# Revit family: Curved Walls U-Profile
name_source: partatom
category: Generic Models
revit_build: Autodesk Revit 2016 (Build: 20160217_1800(x64)
units: mm (PartAtom-declared; Revit-internal decimal feet)

## family parameters
Always vertical = No
Can host rebar = No
Cut with Voids When Loaded = No
Part Type = Normal
Room Calculation Point = No
Round Connector Dimension = Use Diameter
Shared = No
Work Plane-Based = Yes

## types (2) — shared parameters
B (Min 2", Max A+B+C=54") = 0' - 8"
Default Elevation = 0' - 0"
Description = Prefabricated Drywall Profiles
Manufacturer = Curved Walls Inc
URL = www.curvedwalls.ca

## per-type parameters (varying)
| type | A (Min 2", Max A+B+C=54" | C (Min 2", Max A+B+C=54") | GWB Thickness (1/2", 5/8") |
| 1/2" Thk. x 8" H1 x 8" W x 8" H2 | 0' - 8" | 0' - 8" | 0' - 0 1/2" |
| 5/8" Thk. x 4" H1 x 8" W x 2" H2 | 0' - 4" | 0' - 2" | 0' - 0 5/8" |

## geometry (parser evidence)
native form markers: Blend x4, Sweep x2
no freeform markers — native parametric forms only
